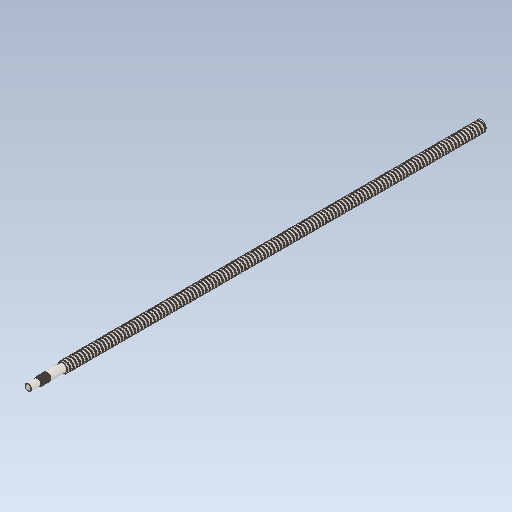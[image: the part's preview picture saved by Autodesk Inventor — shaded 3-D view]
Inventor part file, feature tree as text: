
AUTODESK INVENTOR PART (.ipt)
format: ipt  version: 2020.1 (Build 241239000, 239)  size: 3,923,456 bytes
history: native  units: mm
features: other x2, extrude x1, sketch x1
ambient origin geometry x8: Origin, YZ Plane, XZ Plane, XY Plane, X Axis, Y Axis, Z Axis, Center Point
bodies: Body1 (feature_tree)
feature tree (4):
  other  "Твердое тело1"
  extrude  "Выдавливание1"  Depth=100.0mm TaperAngle=0.0deg
  sketch  "Эскиз1"
  other  "Aesthetic Chamfer"
